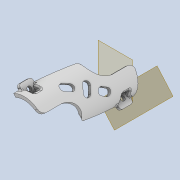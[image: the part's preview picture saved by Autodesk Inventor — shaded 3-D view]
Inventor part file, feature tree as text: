
AUTODESK INVENTOR PART (.ipt)
format: ipt  version: 2020 (Build 240168000, 168)  size: 612,864 bytes
history: native  units: mm
features: sketch x12, extrude x11, fillet x8, projected_geometry x8, reference x7, other x6, plane x4, chamfer x3, thicken_offset x1, hole x1
ambient origin geometry x8: Origin, YZ Plane, XZ Plane, XY Plane, X Axis, Y Axis, Z Axis, Center Point
bodies: Body1 (feature_tree)
feature tree (61):
  plane  "Work Plane1"
  sketch  "Sketch2"  dims[d6=1.5mm d7=1.0mm]
  plane  "Work Plane2"
  extrude  "Extrusion2"  Depth=1.0mm
  extrude  "Extrusion3"  Depth=4.0mm
  extrude  "Extrusion4"  Depth=2.0mm
  extrude  "Extrusion5"  Depth=4.0mm TaperAngle=0.0deg
  chamfer  "Chamfer1"  Distance=4.0mm
  chamfer  "Chamfer2"  Distance=3.0mm Angle=45.0deg
  plane  "Work Plane3"
  plane  "Work Plane4"
  extrude  "Extrusion6"  Depth=5.0mm
  extrude  "Extrusion7"  Depth=1.2mm TaperAngle=0.0deg
  extrude  "Extrusion8"  Depth=1.0mm
  thicken_offset  "Thicken1"
  extrude  "Extrusion9"  Depth=1.0mm
  extrude  "Extrusion10"  Depth=4.0mm TaperAngle=0.0deg
  extrude  "Extrusion11"  Depth=0.2mm
  hole  "Hole1"  [1 undecoded]
  fillet  "Fillet2"  Radius=1.2mm
  fillet  "Fillet3"  Radius=1.2mm
  fillet  "Fillet4"  Radius=1.0mm
  fillet  "Fillet5"  Radius=1.0mm
  fillet  "Fillet6"  Radius=1.0mm
  chamfer  "Chamfer3"  Distance=9.0mm
  fillet  "Fillet7"  Radius=1.0mm
  fillet  "Fillet8"  Radius=1.0mm
  fillet  "Fillet9"  Radius=1.0mm
  extrude  "Extrusion12"  Depth=2.5mm
  reference  "Reference4"
  reference  "Reference5"
  sketch  "Sketch3"  dims[d8=2.0mm d9=4.0mm]
  reference  "Reference6"
  sketch  "Sketch4"  dims[d10=35.0mm d11=0.0mm d12=2.0mm]
  projected_geometry  "Projected Loop1"
  sketch  "Sketch5"  dims[d13=17.5mm d14=0.0mm d15=4.0mm d16=0.0mm d17=4.0mm d18=0.0mm d19=3.0mm d20=14.0mm d21=45.0deg]
  projected_geometry  "Projected Loop2"
  sketch  "Sketch6"  dims[d22=3.0mm d23=14.0mm d24=45.0deg d25=5.0mm]
  reference  "Reference7"
  sketch  "Sketch7"  dims[d26=5.0mm d27=1.2mm d28=0.0mm]
  projected_geometry  "Projected Loop3"
  sketch  "Sketch8"  dims[d29=1.8mm d30=0.0mm d31=1.0mm]
  projected_geometry  "Projected Loop4"
  sketch  "Sketch9"  dims[d32=1.0mm d33=1.0mm]
  reference  "Reference8"
  sketch  "Sketch10"  dims[d34=1.0mm d35=4.0mm d36=0.0mm]
  projected_geometry  "Projected Loop5"
  sketch  "Sketch11"  dims[d37=0.2mm d38=0.2mm]
  projected_geometry  "Projected Loop6"
  sketch  "Sketch12"  dims[d39=5.0mm d40=5.0mm d41=1.2mm d42=0.0mm d43=1.2mm d44=0.0mm d45=1.0mm d46=1.0mm d47=1.0mm]
  reference  "Reference9"
  reference  "Reference10"
  sketch  "Sketch13"  dims[d48=1.0mm d49=9.0mm d50=0.0mm d51=1.6mm d52=6.0mm d53=4.0mm d54=2.0mm d55=90.0deg d56=100.0mm d57=0.0mm d59=1.0mm d60=1.0mm d61=1.0mm d62=0.5mm d63=0.5mm d64=0.5mm d65=14.0mm d66=45.0deg d67=6.0mm d68=1.0mm d69=2.0mm d70=9.0mm d71=9.0mm d72=1.2mm d73=2.5mm d74=1.0mm d75=2.5mm d76=1.0mm d77=2.5mm d78=9.0mm d79=0.0mm]
  projected_geometry  "Projected Loop7"
  projected_geometry  "Projected Loop8"
  parser-record x1  (decoder bookkeeping rows leaked as tree rows — omitted from the tree; the rows remain in map.json)
  other  "tip2_ass_t1.iam"
  other  "bearing_holder_2:1"
  other  "cab_coil_1:2"
  other  "cable_holder_1:1"
  other  "cab_coil_1:1"
note: 1 required parameter value undecoded (feature->parameter linkage not recoverable at this tier; creation-order binding heuristic only, values carry confidence <= 0.55)
note: 1 file-system path scrubbed to <path> (originals preserved in map.json)
